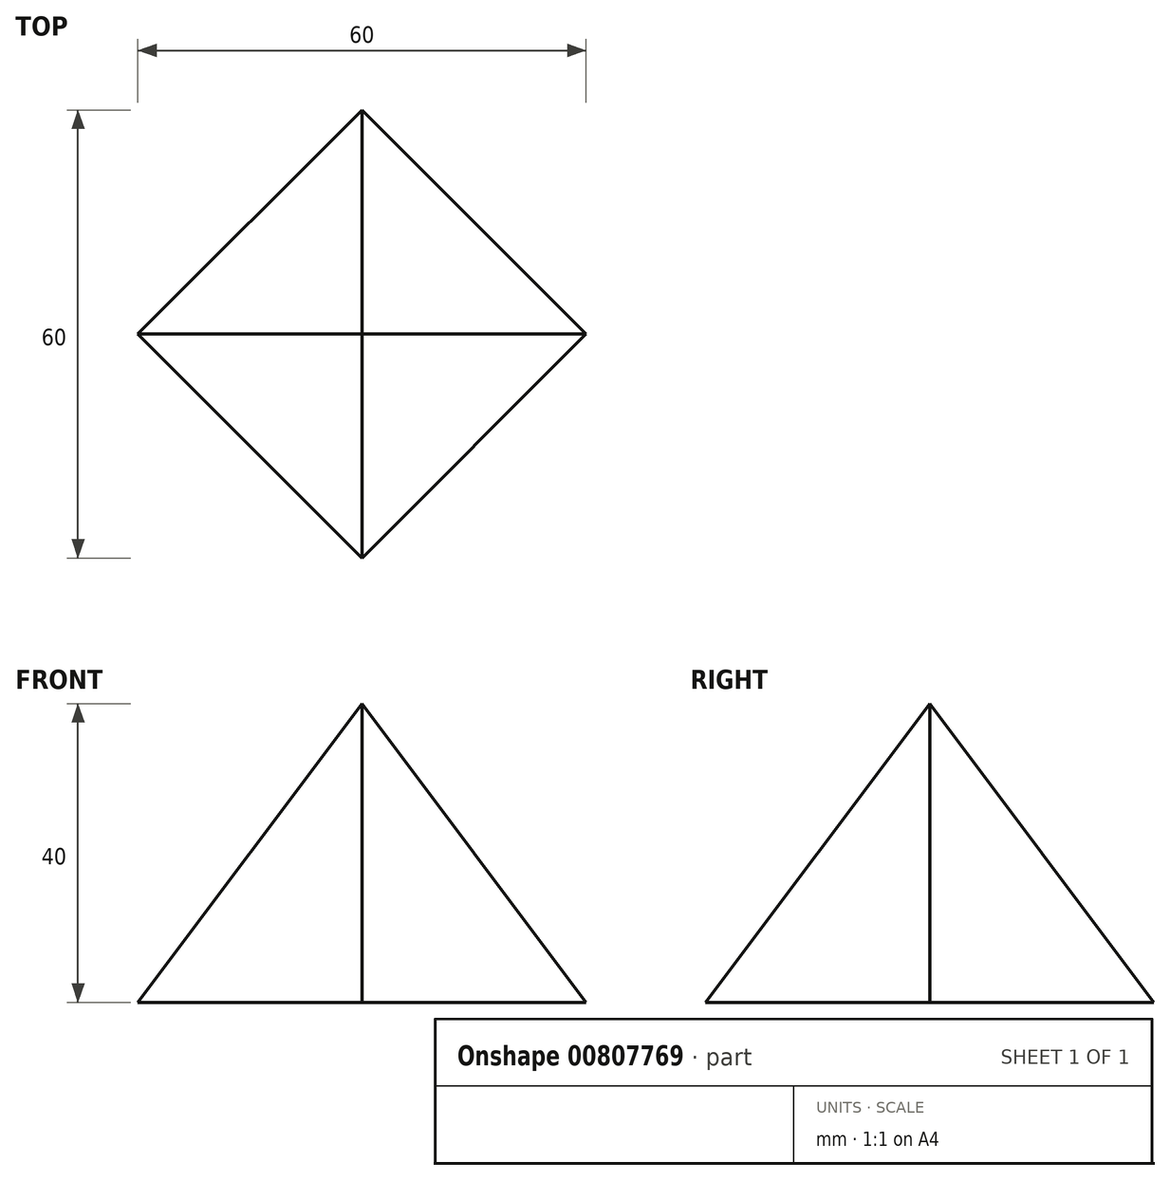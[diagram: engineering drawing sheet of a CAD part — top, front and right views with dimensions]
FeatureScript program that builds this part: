
annotation { "Feature Type Name" : "Feature", "Feature Type Description" : "" }
export const myFeature = defineFeature(function(context is Context, id is Id, definition is map)
    precondition{}
    {
        {
            var Q0;
            Q0=qCreatedBy(makeId("Top.planeOp"),FACE);
            var sketch = newSketch(context, id + "F0", { "sketchPlane" : qUnion([Q0])});
            skLineSegment(sketch, "E0.bottom", {"start": v(-30, 30) * mm, "end": v(30, 30) * mm});
            skLineSegment(sketch, "E0.top", {"start": v(-30, -30) * mm, "end": v(30, -30) * mm});
            skLineSegment(sketch, "E0.left", {"start": v(-30, 30) * mm, "end": v(-30, -30) * mm});
            skLineSegment(sketch, "E0.right", {"start": v(30, 30) * mm, "end": v(30, -30) * mm});
            skPoint(sketch, "E0.middle", {"position": v(0, 0) * mm});
            skLineSegment(sketch, "E1", {"start": v(-30, 0) * mm, "end": v(0, 30) * mm});
            skLineSegment(sketch, "E2", {"start": v(0, 30) * mm, "end": v(30, 0) * mm});
            skLineSegment(sketch, "E3", {"start": v(30, 0) * mm, "end": v(0, -30) * mm});
            skLineSegment(sketch, "E4", {"start": v(0, -30) * mm, "end": v(-30, 0) * mm});
            skSolve(sketch);
        }
        {
            var Q0;
            Q0=qCreatedBy(makeId("Top.planeOp"),FACE);
            cPlane(context, id + "F1", {"entities" : qUnion([Q0]), "cplaneType" : CPlaneType.OFFSET, "offset" : 40 * mm, "width" : 150 * mm, "height" : 150 * mm});
        }
        {
            var Q0;
            Q0=qCreatedBy(id+"F1.planeOp",FACE);
            var sketch = newSketch(context, id + "F2", { "sketchPlane" : qUnion([Q0])});
            skPoint(sketch, "E5.0", {"position": v(0, 0) * mm});
            skSolve(sketch);
        }
        {
            var Q0;
            Q0=makeQuery(id+"F0.imprint","IMPRINT",FACE,{"disambiguationData":[TD([[makeQuery(id+"F0.imprint","IMPRINT",EDGE,{"derivedFrom":sQuery(id+"F0.wireOp",EDGE,"E1")}),-1.0]])]});
            var Q1;
            Q1=sQuery(id+"F2.wireOp",VERTEX,"E5.0");
            loft(context, id + "F3", {"sheetProfilesArray" : [{ "sheetProfileEntities" : qUnion([Q0]) }, { "sheetProfileEntities" : qUnion([Q1]) }]});
        }
    });
